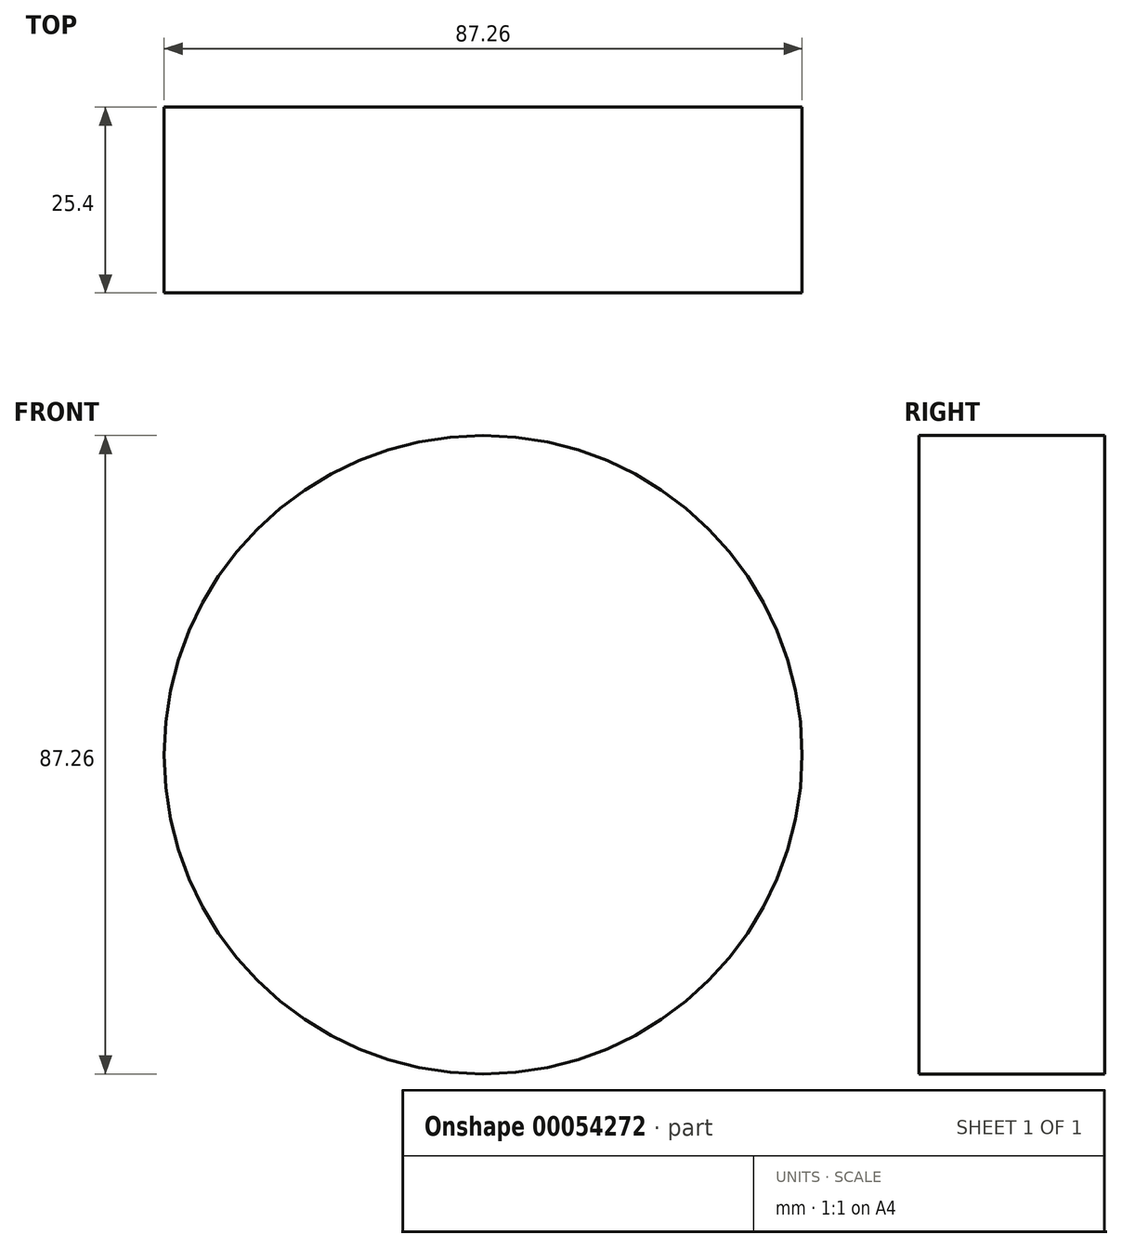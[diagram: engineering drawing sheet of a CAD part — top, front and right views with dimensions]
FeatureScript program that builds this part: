
annotation { "Feature Type Name" : "Feature", "Feature Type Description" : "" }
export const myFeature = defineFeature(function(context is Context, id is Id, definition is map)
    precondition{}
    {
        {
            var Q0;
            Q0=qCreatedBy(makeId("Front.planeOp"),FACE);
            var sketch = newSketch(context, id + "F0", { "sketchPlane" : qUnion([Q0])});
            skCircle(sketch, "E0", {"center": v(0, 0) * mm, "radius": 43.63 * mm});
            skSolve(sketch);
        }
        {
            var Q0;
            Q0 = qSketchRegion(id + "F0", true);
            var Q1;
            Q1=makeQuery(id+"F0.imprint","IMPRINT",FACE,{"disambiguationData":[TD([[makeQuery(id+"F0.imprint","IMPRINT",EDGE,{"derivedFrom":sQuery(id+"F0.wireOp",EDGE,"E0")}),1.0]])]});
            extrude(context, id + "F1", {"entities" : qUnion([Q0, Q1]), "depth" : 25.4 * mm});
        }
    });
